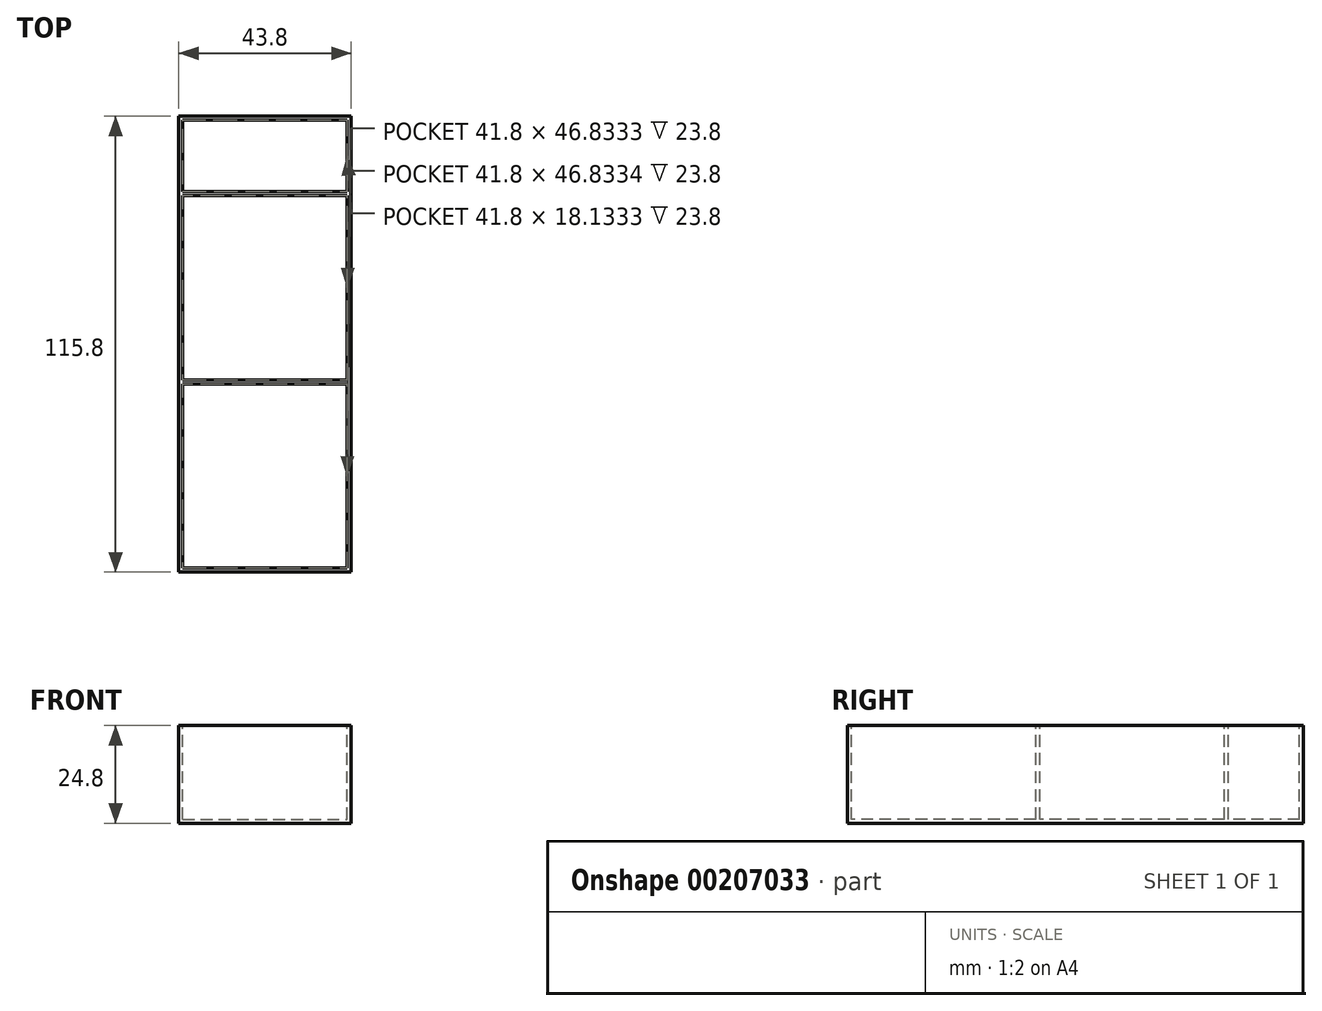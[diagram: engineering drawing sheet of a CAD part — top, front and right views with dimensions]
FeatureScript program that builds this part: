
annotation { "Feature Type Name" : "Feature", "Feature Type Description" : "" }
export const myFeature = defineFeature(function(context is Context, id is Id, definition is map)
    precondition{}
    {
        {
            var Q0;
            Q0=qCreatedBy(makeId("Top.planeOp"),FACE);
            var sketch = newSketch(context, id + "F0", { "sketchPlane" : qUnion([Q0])});
            skLineSegment(sketch, "E0.bottom", {"start": v(0, 0) * mm, "end": v(43.8, 0) * mm});
            skLineSegment(sketch, "E0.top", {"start": v(0, -115.8) * mm, "end": v(43.8, -115.8) * mm});
            skLineSegment(sketch, "E0.left", {"start": v(0, 0) * mm, "end": v(0, -115.8) * mm});
            skLineSegment(sketch, "E0.right", {"start": v(43.8, 0) * mm, "end": v(43.8, -115.8) * mm});
            skPoint(sketch, "E1.visualSharp", {"position": v(0, 0) * mm});
            skPoint(sketch, "E2.visualSharp", {"position": v(43.8, 0) * mm});
            skPoint(sketch, "E3.visualSharp", {"position": v(43.8, -115.8) * mm});
            skPoint(sketch, "E4.visualSharp", {"position": v(0, -115.8) * mm});
            skSolve(sketch);
        }
        {
            var Q0;
            Q0=makeQuery(id+"F0.imprint","IMPRINT",FACE,{"disambiguationData":[TD([[makeQuery(id+"F0.imprint","IMPRINT",EDGE,{"derivedFrom":sQuery(id+"F0.wireOp",EDGE,"E0.bottom")}),-1.0]])]});
            extrude(context, id + "F1", {"entities" : qUnion([Q0]), "depth" : 24.8 * mm});
        }
        {
            var Q0;
            Q0=makeQuery(id+"F1.opExtrude","CAP_FACE",FACE,{"disambiguationData":[OSD([sQuery(id+"F0.wireOp",EDGE,"E0.bottom"),sQuery(id+"F0.wireOp",EDGE,"E0.top"),sQuery(id+"F0.wireOp",EDGE,"E0.left"),sQuery(id+"F0.wireOp",EDGE,"E0.right")])],"isStart":false});
            var sketch = newSketch(context, id + "F2", { "sketchPlane" : qUnion([Q0])});
            skLineSegment(sketch, "E5.bottom", {"start": v(1, -1) * mm, "end": v(42.8, -1) * mm});
            skLineSegment(sketch, "E5.top", {"start": v(1, -19.13) * mm, "end": v(42.8, -19.13) * mm});
            skLineSegment(sketch, "E5.left", {"start": v(1, -1) * mm, "end": v(1, -19.13) * mm});
            skLineSegment(sketch, "E5.right", {"start": v(42.8, -1) * mm, "end": v(42.8, -19.13) * mm});
            skLineSegment(sketch, "E6.bottom", {"start": v(1, -20.13) * mm, "end": v(42.8, -20.13) * mm});
            skLineSegment(sketch, "E6.top", {"start": v(1, -66.97) * mm, "end": v(42.8, -66.97) * mm});
            skLineSegment(sketch, "E6.left", {"start": v(1, -20.13) * mm, "end": v(1, -66.97) * mm});
            skLineSegment(sketch, "E6.right", {"start": v(42.8, -20.13) * mm, "end": v(42.8, -66.97) * mm});
            skLineSegment(sketch, "E7.bottom", {"start": v(1, -67.97) * mm, "end": v(42.8, -67.97) * mm});
            skLineSegment(sketch, "E7.top", {"start": v(1, -114.8) * mm, "end": v(42.8, -114.8) * mm});
            skLineSegment(sketch, "E7.left", {"start": v(1, -67.97) * mm, "end": v(1, -114.8) * mm});
            skLineSegment(sketch, "E7.right", {"start": v(42.8, -67.97) * mm, "end": v(42.8, -114.8) * mm});
            skPoint(sketch, "E8.visualSharp", {"position": v(1, -1) * mm});
            skPoint(sketch, "E9.visualSharp", {"position": v(42.8, -1) * mm});
            skPoint(sketch, "E10.visualSharp", {"position": v(42.8, -19.13) * mm});
            skPoint(sketch, "E11.visualSharp", {"position": v(1, -19.13) * mm});
            skPoint(sketch, "E12.visualSharp", {"position": v(1, -20.13) * mm});
            skPoint(sketch, "E13.visualSharp", {"position": v(42.8, -20.13) * mm});
            skPoint(sketch, "E14.visualSharp", {"position": v(42.8, -66.97) * mm});
            skPoint(sketch, "E15.visualSharp", {"position": v(1, -66.97) * mm});
            skPoint(sketch, "E16.visualSharp", {"position": v(1, -67.97) * mm});
            skPoint(sketch, "E17.visualSharp", {"position": v(42.8, -114.8) * mm});
            skPoint(sketch, "E18.visualSharp", {"position": v(1, -114.8) * mm});
            skSolve(sketch);
        }
        {
            var Q0;
            Q0=makeQuery(id+"F2.imprint","IMPRINT",FACE,{"disambiguationData":[TD([[makeQuery(id+"F2.imprint","IMPRINT",EDGE,{"derivedFrom":sQuery(id+"F2.wireOp",EDGE,"E5.bottom")}),-1.0]])]});
            var Q1;
            Q1=makeQuery(id+"F2.imprint","IMPRINT",FACE,{"disambiguationData":[TD([[makeQuery(id+"F2.imprint","IMPRINT",EDGE,{"derivedFrom":sQuery(id+"F2.wireOp",EDGE,"E6.bottom")}),-1.0]])]});
            var Q2;
            Q2=makeQuery(id+"F2.imprint","IMPRINT",FACE,{"disambiguationData":[TD([[makeQuery(id+"F2.imprint","IMPRINT",EDGE,{"derivedFrom":sQuery(id+"F2.wireOp",EDGE,"E7.bottom")}),-1.0]])]});
            extrude(context, id + "F3", {"entities" : qUnion([Q0, Q1, Q2]), "operationType" : NewBodyOperationType.REMOVE, "oppositeDirection" : true, "depth" : 23.8 * mm});
        }
    });
